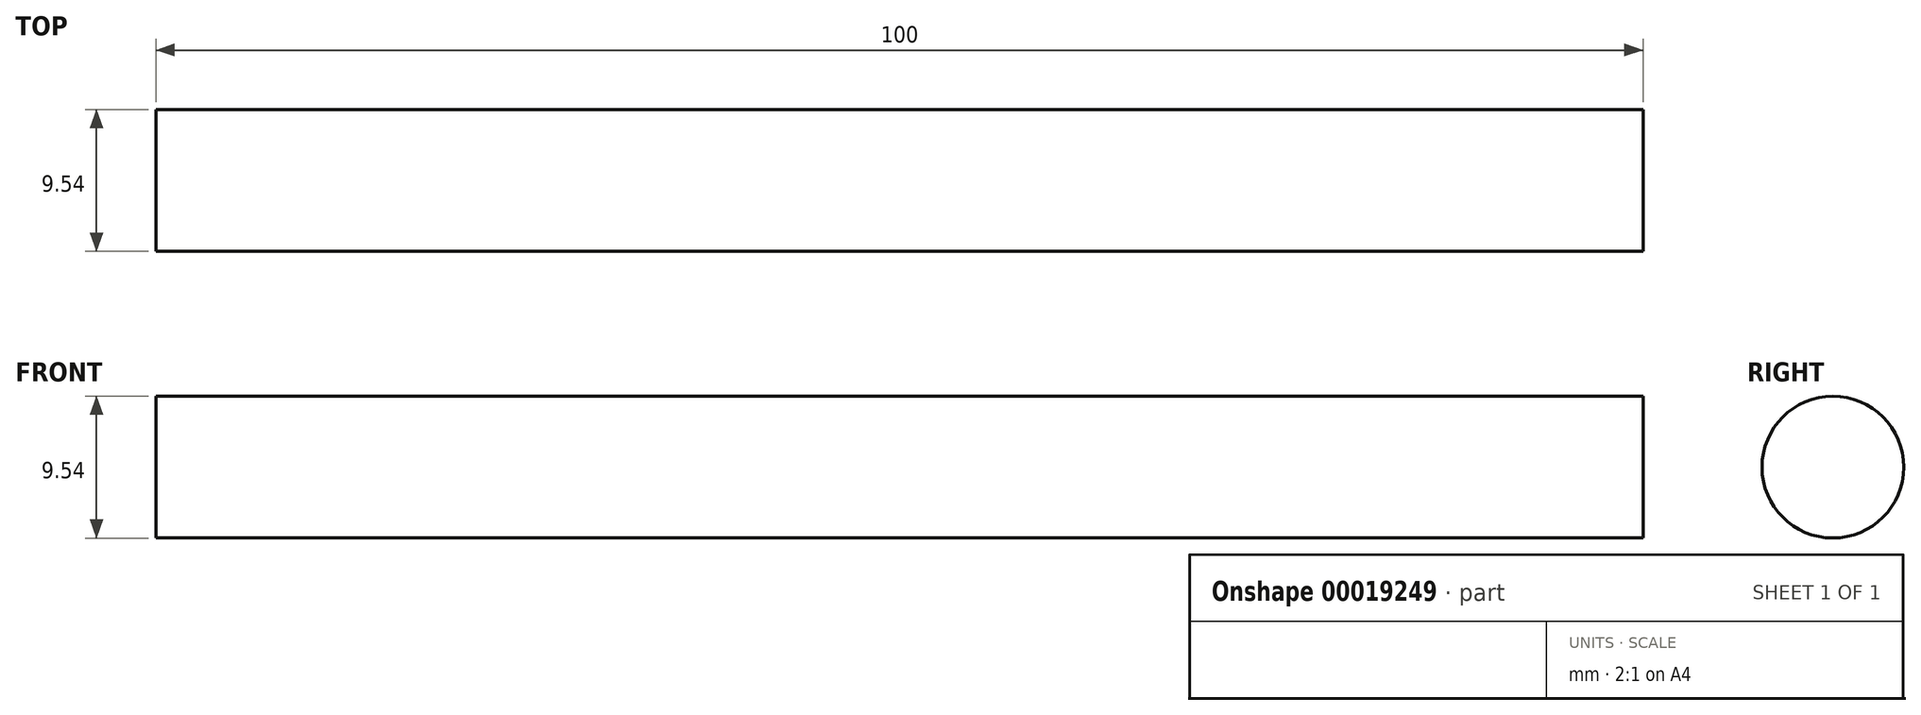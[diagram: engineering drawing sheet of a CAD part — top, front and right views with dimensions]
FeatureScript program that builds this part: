
annotation { "Feature Type Name" : "Feature", "Feature Type Description" : "" }
export const myFeature = defineFeature(function(context is Context, id is Id, definition is map)
    precondition{}
    {
        {
            var Q0;
            Q0=qCreatedBy(makeId("Right.planeOp"),FACE);
            var sketch = newSketch(context, id + "F0", { "sketchPlane" : qUnion([Q0])});
            skCircle(sketch, "E0", {"center": v(0, 0) * mm, "radius": 4.77 * mm});
            skSolve(sketch);
        }
        {
            var Q0;
            Q0=makeQuery(id+"F0.imprint","IMPRINT",FACE,{"disambiguationData":[TD([[makeQuery(id+"F0.imprint","IMPRINT",EDGE,{"derivedFrom":sQuery(id+"F0.wireOp",EDGE,"E0")}),1.0]])]});
            extrude(context, id + "F1", {"entities" : qUnion([Q0]), "depth" : 100 * mm});
        }
    });
